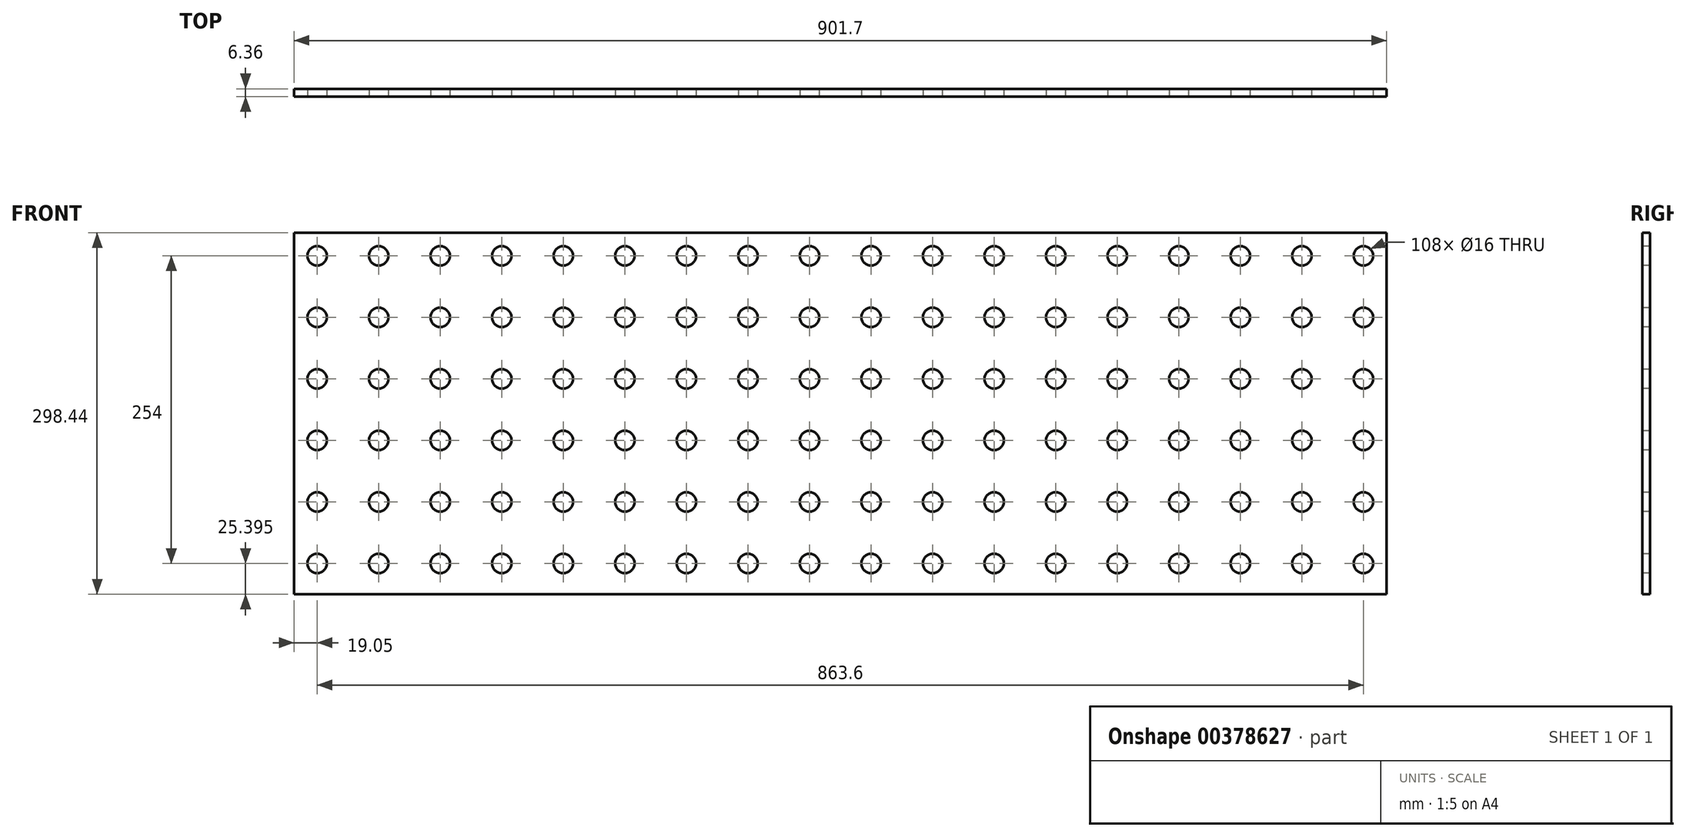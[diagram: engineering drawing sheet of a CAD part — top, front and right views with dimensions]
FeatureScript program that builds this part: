
annotation { "Feature Type Name" : "Feature", "Feature Type Description" : "" }
export const myFeature = defineFeature(function(context is Context, id is Id, definition is map)
    precondition{}
    {
        {
            var Q0;
            Q0=qCreatedBy(makeId("Front.planeOp"),FACE);
            var sketch = newSketch(context, id + "F0", { "sketchPlane" : qUnion([Q0])});
            skLineSegment(sketch, "E0.bottom", {"start": v(450.85, 149.23) * mm, "end": v(-450.85, 149.23) * mm});
            skLineSegment(sketch, "E0.top", {"start": v(450.85, -149.23) * mm, "end": v(-450.85, -149.23) * mm});
            skLineSegment(sketch, "E0.left", {"start": v(450.85, 149.23) * mm, "end": v(450.85, -149.23) * mm});
            skLineSegment(sketch, "E0.right", {"start": v(-450.85, 149.23) * mm, "end": v(-450.85, -149.23) * mm});
            skPoint(sketch, "E0.middle", {"position": v(0, 0) * mm});
            skSolve(sketch);
        }
        {
            var Q0;
            Q0 = qSketchRegion(id + "F0", true);
            extrude(context, id + "F1", {"entities" : qUnion([Q0]), "endBound" : BoundingType.SYMMETRIC, "depth" : 6.35 * mm});
        }
        {
            var Q0;
            Q0=makeQuery(id+"F1.opExtrude","CAP_FACE",FACE,{"disambiguationData":[OSD([sQuery(id+"F0.wireOp",EDGE,"E0.bottom"),sQuery(id+"F0.wireOp",EDGE,"E0.top"),sQuery(id+"F0.wireOp",EDGE,"E0.left"),sQuery(id+"F0.wireOp",EDGE,"E0.right")])],"isStart":false});
            var sketch = newSketch(context, id + "F2", { "sketchPlane" : qUnion([Q0])});
            skCircle(sketch, "E1", {"center": v(-431.8, -123.83) * mm, "radius": 8 * mm});
            skCircle(sketch, "E2.0.1.0", {"center": v(-431.8, -73.03) * mm, "radius": 8 * mm});
            skCircle(sketch, "E2.0.2.0", {"center": v(-431.8, -22.22) * mm, "radius": 8 * mm});
            skCircle(sketch, "E2.0.3.0", {"center": v(-431.8, 28.58) * mm, "radius": 8 * mm});
            skCircle(sketch, "E2.0.4.0", {"center": v(-431.8, 79.38) * mm, "radius": 8 * mm});
            skCircle(sketch, "E2.0.5.0", {"center": v(-431.8, 130.18) * mm, "radius": 8 * mm});
            skCircle(sketch, "E2.1.0.0", {"center": v(-381, -123.83) * mm, "radius": 8 * mm});
            skCircle(sketch, "E2.1.1.0", {"center": v(-381, -73.03) * mm, "radius": 8 * mm});
            skCircle(sketch, "E2.1.2.0", {"center": v(-381, -22.22) * mm, "radius": 8 * mm});
            skCircle(sketch, "E2.1.3.0", {"center": v(-381, 28.58) * mm, "radius": 8 * mm});
            skCircle(sketch, "E2.1.4.0", {"center": v(-381, 79.38) * mm, "radius": 8 * mm});
            skCircle(sketch, "E2.1.5.0", {"center": v(-381, 130.18) * mm, "radius": 8 * mm});
            skCircle(sketch, "E2.2.0.0", {"center": v(-330.2, -123.83) * mm, "radius": 8 * mm});
            skCircle(sketch, "E2.2.1.0", {"center": v(-330.2, -73.03) * mm, "radius": 8 * mm});
            skCircle(sketch, "E2.2.2.0", {"center": v(-330.2, -22.22) * mm, "radius": 8 * mm});
            skCircle(sketch, "E2.2.3.0", {"center": v(-330.2, 28.58) * mm, "radius": 8 * mm});
            skCircle(sketch, "E2.2.4.0", {"center": v(-330.2, 79.38) * mm, "radius": 8 * mm});
            skCircle(sketch, "E2.2.5.0", {"center": v(-330.2, 130.18) * mm, "radius": 8 * mm});
            skCircle(sketch, "E2.3.0.0", {"center": v(-279.4, -123.83) * mm, "radius": 8 * mm});
            skCircle(sketch, "E2.3.1.0", {"center": v(-279.4, -73.03) * mm, "radius": 8 * mm});
            skCircle(sketch, "E2.3.2.0", {"center": v(-279.4, -22.22) * mm, "radius": 8 * mm});
            skCircle(sketch, "E2.3.3.0", {"center": v(-279.4, 28.58) * mm, "radius": 8 * mm});
            skCircle(sketch, "E2.3.4.0", {"center": v(-279.4, 79.38) * mm, "radius": 8 * mm});
            skCircle(sketch, "E2.3.5.0", {"center": v(-279.4, 130.18) * mm, "radius": 8 * mm});
            skCircle(sketch, "E2.4.0.0", {"center": v(-228.6, -123.83) * mm, "radius": 8 * mm});
            skCircle(sketch, "E2.4.1.0", {"center": v(-228.6, -73.03) * mm, "radius": 8 * mm});
            skCircle(sketch, "E2.4.2.0", {"center": v(-228.6, -22.22) * mm, "radius": 8 * mm});
            skCircle(sketch, "E2.4.3.0", {"center": v(-228.6, 28.58) * mm, "radius": 8 * mm});
            skCircle(sketch, "E2.4.4.0", {"center": v(-228.6, 79.38) * mm, "radius": 8 * mm});
            skCircle(sketch, "E2.4.5.0", {"center": v(-228.6, 130.18) * mm, "radius": 8 * mm});
            skCircle(sketch, "E2.5.0.0", {"center": v(-177.8, -123.83) * mm, "radius": 8 * mm});
            skCircle(sketch, "E2.5.1.0", {"center": v(-177.8, -73.03) * mm, "radius": 8 * mm});
            skCircle(sketch, "E2.5.2.0", {"center": v(-177.8, -22.22) * mm, "radius": 8 * mm});
            skCircle(sketch, "E2.5.3.0", {"center": v(-177.8, 28.58) * mm, "radius": 8 * mm});
            skCircle(sketch, "E2.5.4.0", {"center": v(-177.8, 79.38) * mm, "radius": 8 * mm});
            skCircle(sketch, "E2.5.5.0", {"center": v(-177.8, 130.18) * mm, "radius": 8 * mm});
            skCircle(sketch, "E2.6.0.0", {"center": v(-127, -123.83) * mm, "radius": 8 * mm});
            skCircle(sketch, "E2.6.1.0", {"center": v(-127, -73.03) * mm, "radius": 8 * mm});
            skCircle(sketch, "E2.6.2.0", {"center": v(-127, -22.22) * mm, "radius": 8 * mm});
            skCircle(sketch, "E2.6.3.0", {"center": v(-127, 28.58) * mm, "radius": 8 * mm});
            skCircle(sketch, "E2.6.4.0", {"center": v(-127, 79.38) * mm, "radius": 8 * mm});
            skCircle(sketch, "E2.6.5.0", {"center": v(-127, 130.18) * mm, "radius": 8 * mm});
            skCircle(sketch, "E2.7.0.0", {"center": v(-76.2, -123.83) * mm, "radius": 8 * mm});
            skCircle(sketch, "E2.7.1.0", {"center": v(-76.2, -73.03) * mm, "radius": 8 * mm});
            skCircle(sketch, "E2.7.2.0", {"center": v(-76.2, -22.22) * mm, "radius": 8 * mm});
            skCircle(sketch, "E2.7.3.0", {"center": v(-76.2, 28.58) * mm, "radius": 8 * mm});
            skCircle(sketch, "E2.7.4.0", {"center": v(-76.2, 79.38) * mm, "radius": 8 * mm});
            skCircle(sketch, "E2.7.5.0", {"center": v(-76.2, 130.18) * mm, "radius": 8 * mm});
            skCircle(sketch, "E2.8.0.0", {"center": v(-25.4, -123.83) * mm, "radius": 8 * mm});
            skCircle(sketch, "E2.8.1.0", {"center": v(-25.4, -73.03) * mm, "radius": 8 * mm});
            skCircle(sketch, "E2.8.2.0", {"center": v(-25.4, -22.22) * mm, "radius": 8 * mm});
            skCircle(sketch, "E2.8.3.0", {"center": v(-25.4, 28.58) * mm, "radius": 8 * mm});
            skCircle(sketch, "E2.8.4.0", {"center": v(-25.4, 79.38) * mm, "radius": 8 * mm});
            skCircle(sketch, "E2.8.5.0", {"center": v(-25.4, 130.18) * mm, "radius": 8 * mm});
            skCircle(sketch, "E2.9.0.0", {"center": v(25.4, -123.83) * mm, "radius": 8 * mm});
            skCircle(sketch, "E2.9.1.0", {"center": v(25.4, -73.03) * mm, "radius": 8 * mm});
            skCircle(sketch, "E2.9.2.0", {"center": v(25.4, -22.22) * mm, "radius": 8 * mm});
            skCircle(sketch, "E2.9.3.0", {"center": v(25.4, 28.58) * mm, "radius": 8 * mm});
            skCircle(sketch, "E2.9.4.0", {"center": v(25.4, 79.38) * mm, "radius": 8 * mm});
            skCircle(sketch, "E2.9.5.0", {"center": v(25.4, 130.18) * mm, "radius": 8 * mm});
            skCircle(sketch, "E2.10.0.0", {"center": v(76.2, -123.83) * mm, "radius": 8 * mm});
            skCircle(sketch, "E2.10.1.0", {"center": v(76.2, -73.03) * mm, "radius": 8 * mm});
            skCircle(sketch, "E2.10.2.0", {"center": v(76.2, -22.22) * mm, "radius": 8 * mm});
            skCircle(sketch, "E2.10.3.0", {"center": v(76.2, 28.58) * mm, "radius": 8 * mm});
            skCircle(sketch, "E2.10.4.0", {"center": v(76.2, 79.38) * mm, "radius": 8 * mm});
            skCircle(sketch, "E2.10.5.0", {"center": v(76.2, 130.18) * mm, "radius": 8 * mm});
            skCircle(sketch, "E2.11.0.0", {"center": v(127, -123.83) * mm, "radius": 8 * mm});
            skCircle(sketch, "E2.11.1.0", {"center": v(127, -73.03) * mm, "radius": 8 * mm});
            skCircle(sketch, "E2.11.2.0", {"center": v(127, -22.22) * mm, "radius": 8 * mm});
            skCircle(sketch, "E2.11.3.0", {"center": v(127, 28.58) * mm, "radius": 8 * mm});
            skCircle(sketch, "E2.11.4.0", {"center": v(127, 79.38) * mm, "radius": 8 * mm});
            skCircle(sketch, "E2.11.5.0", {"center": v(127, 130.18) * mm, "radius": 8 * mm});
            skCircle(sketch, "E2.12.0.0", {"center": v(177.8, -123.83) * mm, "radius": 8 * mm});
            skCircle(sketch, "E2.12.1.0", {"center": v(177.8, -73.03) * mm, "radius": 8 * mm});
            skCircle(sketch, "E2.12.2.0", {"center": v(177.8, -22.22) * mm, "radius": 8 * mm});
            skCircle(sketch, "E2.12.3.0", {"center": v(177.8, 28.58) * mm, "radius": 8 * mm});
            skCircle(sketch, "E2.12.4.0", {"center": v(177.8, 79.38) * mm, "radius": 8 * mm});
            skCircle(sketch, "E2.12.5.0", {"center": v(177.8, 130.18) * mm, "radius": 8 * mm});
            skCircle(sketch, "E2.13.0.0", {"center": v(228.6, -123.83) * mm, "radius": 8 * mm});
            skCircle(sketch, "E2.13.1.0", {"center": v(228.6, -73.03) * mm, "radius": 8 * mm});
            skCircle(sketch, "E2.13.2.0", {"center": v(228.6, -22.22) * mm, "radius": 8 * mm});
            skCircle(sketch, "E2.13.3.0", {"center": v(228.6, 28.58) * mm, "radius": 8 * mm});
            skCircle(sketch, "E2.13.4.0", {"center": v(228.6, 79.38) * mm, "radius": 8 * mm});
            skCircle(sketch, "E2.13.5.0", {"center": v(228.6, 130.18) * mm, "radius": 8 * mm});
            skCircle(sketch, "E2.14.0.0", {"center": v(279.4, -123.83) * mm, "radius": 8 * mm});
            skCircle(sketch, "E2.14.1.0", {"center": v(279.4, -73.03) * mm, "radius": 8 * mm});
            skCircle(sketch, "E2.14.2.0", {"center": v(279.4, -22.22) * mm, "radius": 8 * mm});
            skCircle(sketch, "E2.14.3.0", {"center": v(279.4, 28.58) * mm, "radius": 8 * mm});
            skCircle(sketch, "E2.14.4.0", {"center": v(279.4, 79.38) * mm, "radius": 8 * mm});
            skCircle(sketch, "E2.14.5.0", {"center": v(279.4, 130.18) * mm, "radius": 8 * mm});
            skCircle(sketch, "E2.15.0.0", {"center": v(330.2, -123.83) * mm, "radius": 8 * mm});
            skCircle(sketch, "E2.15.1.0", {"center": v(330.2, -73.03) * mm, "radius": 8 * mm});
            skCircle(sketch, "E2.15.2.0", {"center": v(330.2, -22.22) * mm, "radius": 8 * mm});
            skCircle(sketch, "E2.15.3.0", {"center": v(330.2, 28.58) * mm, "radius": 8 * mm});
            skCircle(sketch, "E2.15.4.0", {"center": v(330.2, 79.38) * mm, "radius": 8 * mm});
            skCircle(sketch, "E2.15.5.0", {"center": v(330.2, 130.18) * mm, "radius": 8 * mm});
            skCircle(sketch, "E2.16.0.0", {"center": v(381, -123.83) * mm, "radius": 8 * mm});
            skCircle(sketch, "E2.16.1.0", {"center": v(381, -73.03) * mm, "radius": 8 * mm});
            skCircle(sketch, "E2.16.2.0", {"center": v(381, -22.22) * mm, "radius": 8 * mm});
            skCircle(sketch, "E2.16.3.0", {"center": v(381, 28.58) * mm, "radius": 8 * mm});
            skCircle(sketch, "E2.16.4.0", {"center": v(381, 79.38) * mm, "radius": 8 * mm});
            skCircle(sketch, "E2.16.5.0", {"center": v(381, 130.18) * mm, "radius": 8 * mm});
            skCircle(sketch, "E2.17.0.0", {"center": v(431.8, -123.83) * mm, "radius": 8 * mm});
            skCircle(sketch, "E2.17.1.0", {"center": v(431.8, -73.03) * mm, "radius": 8 * mm});
            skCircle(sketch, "E2.17.2.0", {"center": v(431.8, -22.22) * mm, "radius": 8 * mm});
            skCircle(sketch, "E2.17.3.0", {"center": v(431.8, 28.58) * mm, "radius": 8 * mm});
            skCircle(sketch, "E2.17.4.0", {"center": v(431.8, 79.38) * mm, "radius": 8 * mm});
            skCircle(sketch, "E2.17.5.0", {"center": v(431.8, 130.18) * mm, "radius": 8 * mm});
            skLineSegment(sketch, "E2.direction1", {"start": v(-431.8, -123.83) * mm, "end": v(-381, -123.83) * mm, "construction": true});
            skLineSegment(sketch, "E2.direction2", {"start": v(-431.8, -123.83) * mm, "end": v(-431.8, -73.03) * mm, "construction": true});
            skSolve(sketch);
        }
        {
            var Q0;
            Q0 = qSketchRegion(id + "F2", true);
            extrude(context, id + "F3", {"entities" : qUnion([Q0]), "operationType" : NewBodyOperationType.REMOVE, "endBound" : BoundingType.THROUGH_ALL, "oppositeDirection" : true, "depth" : 25.4 * mm});
        }
    });
